# Revit family: 0042388
name_source: partatom
category: Lighting Fixtures
revit_build: Autodesk Revit 2017 (Build: 20190507_1515(x64)
units: mm (PartAtom-declared; Revit-internal decimal feet)

## family parameters
Cut with Voids When Loaded = No
Host = Face
Light Source = Yes
OmniClass Number = 23.80.70.00
OmniClass Title = Lighting
Part Type = Normal
Room Calculation Point = No
Round Connector Dimension = Use Diameter
Shared = No

## types (4) — shared parameters
-LUMDEPTH_SYL = -277 mm
Assembly Code = D5020200
AssetType = Fixed
BOX_WIDTH_SYL = 40 mm  [stored 0.131234 ft]
ClassificationName = Uniclass2015
ClassificationValue = EF_70_80
Color Filter = 16777215
DEPTH_SYL = 298 mm
Default Elevation = 1219 mm
Dimming Lamp Color Temperature Shift = <None>
DocumentationLiterature = http://www.sylvania-lighting.com
ElectricShockClassification = Class II
Emit Shape Visible in Rendering = No
Emit from Circle Diameter = 610 mm
HEIGHTBOTT_SYL = 7 mm  [stored 0.0229659 ft]
HEIGHT_SYL = 33 mm  [stored 0.108268 ft]
IfcExportAs = IfcLightFixtureType
IfcExportType = IfcLightFixtureType
ImpactProtectionIndex = IK03
IngressProtection = IP40/20
Keynote = 16500
LUMDEPTH_SYL = 277 mm
LUMWIDTH_SYL = 277 mm
Lamp = LED
LampColourRenderingIndex = 80
LampMacAdamStep = 6
LampsType = LED
MAINHEIGHT_SYL = 63 mm
Manufacturer = Feilo Sylvania
ManufacturerName = Feilo Sylvania
Material = aluminium,steel housing, other diffuser
Material_1_SYL = <By Category>
Material_2_SYL = <By Category>
Material_3_SYL = <By Category>
Material_4_SYL = <By Category>
NominalDepth = 595 mm
NominalHeight = 35 mm
NominalLength = 595 mm
PowerFactor = 0.95
TOPWIDTH_SYL = 245 mm  [stored 0.803806 ft]
Tilt Angle = -90.00°
Type Image = <None>
URL = http://www.sylvania-lighting.com
Voltage = 0 V
WIDTH_SYL = 298 mm
Weight = 6.285 kg
zero-valued in all types: Cost

## per-type parameters (varying)
| type | Apparent Load | Description | LampColourTemperature | LampNominalLuminous | LuminousEfficacy | Model | ModelNumber | ModelReference | Name | Photometric Web File | PowerConsumption | TypeName |
| 0042390 START PANEL UGR19 600X600 4600LM 830 SSA | 43 VA | START Panel is a range of backlit LED panels used in recessed ceilings. Ideal for general indoor appliactions such as corridors, breakrooms, offices and meeting rooms. Luminaire dimensions are compatible with common ceiling installation, and the shallow design makes it easy to install in low ceilings. 4600Lm; 43W; 107Lm/W; Drive current: 950mA; Average life: 50000Hrs; 3000K; CRI 80; Glare control <19; IK03; IP40 (from the front); SDCM<3; Class II; SylSmart SSA enabled. | 3000 K | 4600 lm | 107 lm/W | START Panel UGR19 600x600 4600Lm 830 SSA | 0042390 | START Panel UGR19 600x600 4600Lm 830 SSA | START Panel UGR19 600x600 4600Lm 830 SSA | 0042390.ies | 43 W | START Panel UGR19 600x600 4600Lm 830 SSA |
| 0042389 START PANEL UGR19 600X600 4000LM 840 SSA | 36 VA | START Panel is a range of backlit LED panels used in recessed ceilings. Ideal for general indoor appliactions such as corridors, breakrooms, offices and meeting rooms. Luminaire dimensions are compatible with common ceiling installation, and the shallow design makes it easy to install in low ceilings. 4000Lm; 36W; 111Lm/W; Drive current: 750mA; Average life: 50000Hrs; 4000K; CRI 80; Glare control <19; IK03; IP40 (from the front); SDCM<3; Class II; SylSmart SSA enabled. | 4000 K | 4000 lm | 111 lm/W | START Panel UGR19 600x600 4000Lm 840 SSA | 0042389 | START Panel UGR19 600x600 4000Lm 840 SSA | START Panel UGR19 600x600 4000Lm 840 SSA | 0042389.ies | 36 W | START Panel UGR19 600x600 4000Lm 840 SSA |
| 0042388 START PANEL UGR19 600X600 3800LM 830 SSA | 36 VA | START Panel is a range of backlit LED panels used in recessed ceilings. Ideal for general indoor appliactions such as corridors, breakrooms, offices and meeting rooms. Luminaire dimensions are compatible with common ceiling installation, and the shallow design makes it easy to install in low ceilings. 3800Lm; 36W; 106Lm/W; Drive current: 750mA; Average life: 50000Hrs; 3000K; CRI 80; Glare control <19; IK03; IP40 (from the front); SDCM<3; Class II; SylSmart SSA enabled. | 3000 K | 3800 lm | 106 lm/W | START Panel UGR19 600x600 3800Lm 830 SSA | 0042388 | START Panel UGR19 600x600 3800Lm 830 SSA | START Panel UGR19 600x600 3800Lm 830 SSA | 0042388.ies | 36 W | START Panel UGR19 600x600 3800Lm 830 SSA |
| 0042391 START PANEL UGR19 600X600 4800LM 840 SSA | 43 VA | START Panel is a range of backlit LED panels used in recessed ceilings. Ideal for general indoor appliactions such as corridors, breakrooms, offices and meeting rooms. Luminaire dimensions are compatible with common ceiling installation, and the shallow design makes it easy to install in low ceilings. 4800Lm; 43W; 112Lm/W; Drive current: 950mA; Average life: 50000Hrs; 4000K; CRI 80; Glare control <19; IK03; IP40 (from the front); SDCM<3; Class II; SylSmart SSA enabled. | 4000 K | 4800 lm | 112 lm/W | START Panel UGR19 600x600 4800Lm 840 SSA | 0042391 | START Panel UGR19 600x600 4800Lm 840 SSA | START Panel UGR19 600x600 4800Lm 840 SSA | 0042391.ies | 43 W | START Panel UGR19 600x600 4800Lm 840 SSA |

note: [stored X ft] marks values corroborated as IEEE doubles in the binary element streams (Revit-internal decimal feet)

## geometry (parser evidence)
native form markers: Sweep x2
no freeform markers — native parametric forms only
